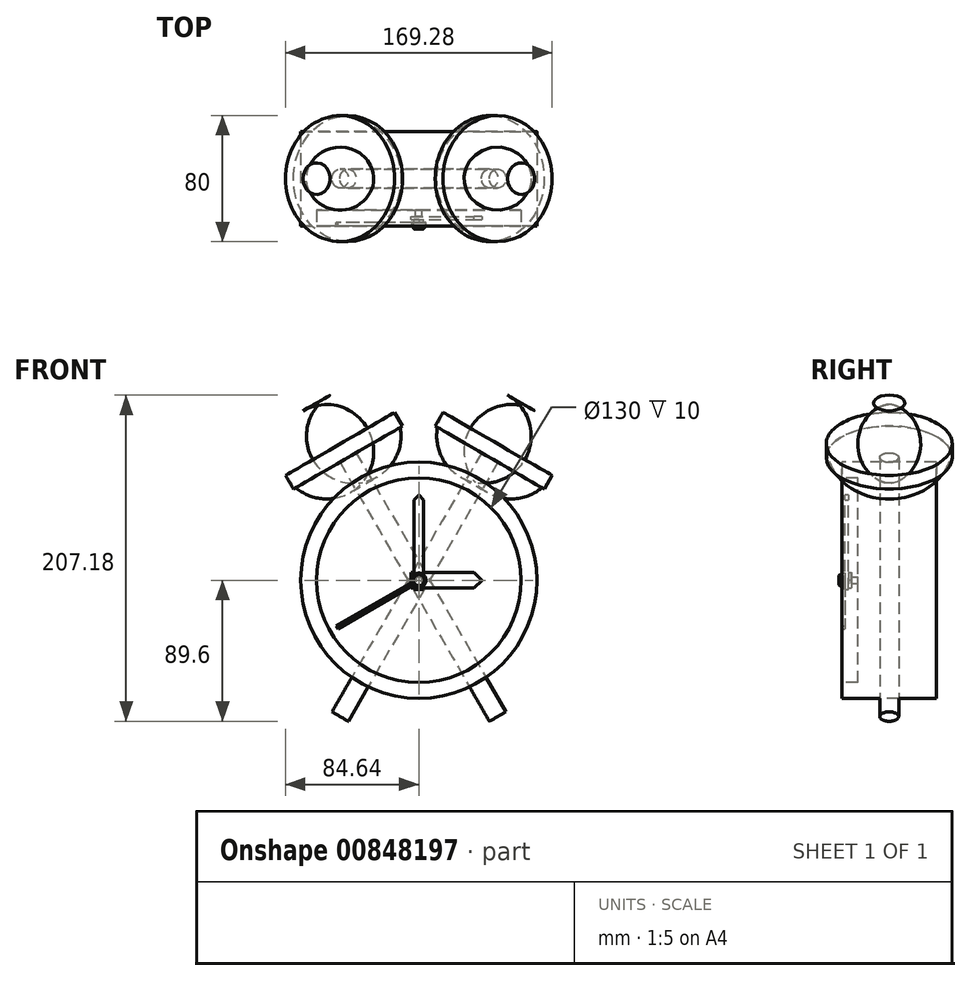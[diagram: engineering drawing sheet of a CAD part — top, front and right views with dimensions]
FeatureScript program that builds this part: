
annotation { "Feature Type Name" : "Feature", "Feature Type Description" : "" }
export const myFeature = defineFeature(function(context is Context, id is Id, definition is map)
    precondition{}
    {
        {
            var Q0;
            Q0=qCreatedBy(makeId("Front.planeOp"),FACE);
            var sketch = newSketch(context, id + "F0", { "sketchPlane" : qUnion([Q0])});
            skCircle(sketch, "E0", {"center": v(0, 0) * mm, "radius": 75 * mm});
            skSolve(sketch);
        }
        {
            var Q0;
            Q0=makeQuery(id+"F0.imprint","IMPRINT",FACE,{"disambiguationData":[TD([[makeQuery(id+"F0.imprint","IMPRINT",EDGE,{"derivedFrom":sQuery(id+"F0.wireOp",EDGE,"E0")}),1.0]])]});
            extrude(context, id + "F1", {"entities" : qUnion([Q0]), "oppositeDirection" : true, "depth" : 60 * mm, "offsetDistance" : 25 * mm});
        }
        {
            var Q0;
            Q0=makeQuery(id+"F1.opExtrude","CAP_FACE",FACE,{"disambiguationData":[OSD([sQuery(id+"F0.wireOp",EDGE,"E0")])],"isStart":true});
            var sketch = newSketch(context, id + "F2", { "sketchPlane" : qUnion([Q0])});
            skCircle(sketch, "E1", {"center": v(0, 0) * mm, "radius": 65 * mm});
            skSolve(sketch);
        }
        {
            var Q0;
            Q0=makeQuery(id+"F2.imprint","IMPRINT",FACE,{"disambiguationData":[TD([[makeQuery(id+"F2.imprint","IMPRINT",EDGE,{"derivedFrom":sQuery(id+"F2.wireOp",EDGE,"E1")}),1.0]])]});
            extrude(context, id + "F3", {"entities" : qUnion([Q0]), "operationType" : NewBodyOperationType.REMOVE, "oppositeDirection" : true, "depth" : 10 * mm, "offsetDistance" : 25 * mm});
        }
        {
            var Q0;
            Q0=makeQuery(id+"F3.boolean.opBoolean","COPY",FACE,{"derivedFrom":makeQuery(id+"F3.opExtrude","CAP_FACE",FACE,{"disambiguationData":[OSD([sQuery(id+"F2.wireOp",EDGE,"E1")])],"isStart":false})});
            var sketch = newSketch(context, id + "F4", { "sketchPlane" : qUnion([Q0])});
            skLineSegment(sketch, "E2", {"start": v(0, 0) * mm, "end": v(0, 130) * mm});
            skLineSegment(sketch, "E3", {"start": v(0, 130) * mm, "end": v(40, 130) * mm});
            skLineSegment(sketch, "E4", {"start": v(40, 130) * mm, "end": v(40, 90) * mm});
            skLineSegment(sketch, "E5", {"start": v(40, 90) * mm, "end": v(6, 90) * mm});
            skLineSegment(sketch, "E6", {"start": v(6, 90) * mm, "end": v(6, -100) * mm});
            skLineSegment(sketch, "E7", {"start": v(6, -100) * mm, "end": v(0, -100) * mm});
            skLineSegment(sketch, "E8", {"start": v(0, -100) * mm, "end": v(0, 0) * mm});
            skSolve(sketch);
        }
        {
            var Q0;
            {var subQ1=sQuery(id+"F4.wireOp",EDGE,"E3");Q0=makeQuery(id+"F4.imprint","IMPRINT",FACE,{"disambiguationData":[TD([[makeQuery(id+"F4.imprint","IMPRINT",EDGE,{"derivedFrom":subQ1}),-1.0]])]});}
            var Q1;
            {var subQ0=sQuery(id+"F4.wireOp",EDGE,"E2");var subQ6=sQuery(id+"F4.wireOp",EDGE,"E8");var subQ7=makeQuery(id+"F4.imprint","INTERSECT",VERTEX,{"derivedFrom":[subQ0,subQ6]});Q1=makeQuery(id+"F4.imprint","IMPRINT",FACE,{"disambiguationData":[TD([[makeQuery(id+"F4.imprint","IMPRINT",EDGE,{"disambiguationData":[TD([[subQ7,-1.0]])],"derivedFrom":subQ0}),-1.0]])]});}
            var Q2;
            {var subQ0=sQuery(id+"F4.wireOp",EDGE,"E7");Q2=makeQuery(id+"F4.imprint","IMPRINT",FACE,{"disambiguationData":[TD([[makeQuery(id+"F4.imprint","IMPRINT",EDGE,{"derivedFrom":subQ0}),-1.0]])]});}
            var Q3;
            Q3=sQuery(id+"F4.wireOp",EDGE,"E2");
            revolve(context, id + "F5", {"surfaceOperationType" : NewSurfaceOperationType.NEW, "entities" : qUnion([Q0, Q1, Q2]), "axis" : qUnion([Q3]), "revolveType" : RevolveType.FULL});
        }
        {
            var Q0;
            Q0=makeQuery(id+"F5.opRevolve","SWEPT_BODY",BODY,{"disambiguationData":[OSD([sQuery(id+"F4.wireOp",EDGE,"E2"),sQuery(id+"F4.wireOp",EDGE,"E3"),sQuery(id+"F4.wireOp",EDGE,"E4"),sQuery(id+"F4.wireOp",EDGE,"E5"),sQuery(id+"F4.wireOp",EDGE,"E6"),sQuery(id+"F4.wireOp",EDGE,"E7"),sQuery(id+"F4.wireOp",EDGE,"E8")])]});
            transform(context, id + "F6", {"entities" : qUnion([Q0]), "transformType" : TransformType.TRANSLATION_3D, "dx" : 0 * mm, "dy" : 20 * mm, "dz" : 0 * mm, "makeCopy" : false});
        }
        {
            var Q0;
            Q0=makeQuery(id+"F5.opRevolve","SWEPT_FACE",FACE,{"disambiguationData":[OSD([sQuery(id+"F4.wireOp",EDGE,"E3")])]});
            fillet(context, id + "F7", {"entities" : qUnion([Q0]), "radius" : 30 * mm, "allowEdgeOverflow" : false});
        }
        {
            var Q0;
            Q0=makeQuery(id+"F5.opRevolve","SWEPT_BODY",BODY,{"disambiguationData":[OSD([sQuery(id+"F4.wireOp",EDGE,"E2"),sQuery(id+"F4.wireOp",EDGE,"E3"),sQuery(id+"F4.wireOp",EDGE,"E4"),sQuery(id+"F4.wireOp",EDGE,"E5"),sQuery(id+"F4.wireOp",EDGE,"E6"),sQuery(id+"F4.wireOp",EDGE,"E7"),sQuery(id+"F4.wireOp",EDGE,"E8")])]});
            var Q1;
            Q1=makeQuery(id+"F1.opExtrude","SWEPT_FACE",FACE,{"disambiguationData":[OSD([sQuery(id+"F0.wireOp",EDGE,"E0")])]});
            transform(context, id + "F8", {"entities" : qUnion([Q0]), "transformType" : TransformType.ROTATION, "transformAxis" : qUnion([Q1]), "angle" : 30 * degree, "makeCopy" : false});
        }
        {
            var Q0;
            Q0=makeQuery(id+"F5.opRevolve","SWEPT_BODY",BODY,{"disambiguationData":[OSD([sQuery(id+"F4.wireOp",EDGE,"E2"),sQuery(id+"F4.wireOp",EDGE,"E3"),sQuery(id+"F4.wireOp",EDGE,"E4"),sQuery(id+"F4.wireOp",EDGE,"E5"),sQuery(id+"F4.wireOp",EDGE,"E6"),sQuery(id+"F4.wireOp",EDGE,"E7"),sQuery(id+"F4.wireOp",EDGE,"E8")])]});
            var Q1;
            Q1=makeQuery(id+"F1.opExtrude","CAP_EDGE",EDGE,{"disambiguationData":[OSD([sQuery(id+"F0.wireOp",EDGE,"E0")])],"isStart":true});
            transform(context, id + "F9", {"entities" : qUnion([Q0]), "transformType" : TransformType.ROTATION, "transformAxis" : qUnion([Q1]), "angle" : 300 * degree, "makeCopy" : true});
        }
        {
            var Q0;
            Q0=makeQuery(id+"F3.boolean.opBoolean","COPY",FACE,{"derivedFrom":makeQuery(id+"F3.opExtrude","CAP_FACE",FACE,{"disambiguationData":[OSD([sQuery(id+"F2.wireOp",EDGE,"E1")])],"isStart":false})});
            var sketch = newSketch(context, id + "F10", { "sketchPlane" : qUnion([Q0])});
            skCircle(sketch, "E9", {"center": v(0, 0) * mm, "radius": 2 * mm});
            skSolve(sketch);
        }
        {
            var Q0;
            Q0=makeQuery(id+"F10.imprint","IMPRINT",FACE,{"disambiguationData":[TD([[makeQuery(id+"F10.imprint","IMPRINT",EDGE,{"derivedFrom":sQuery(id+"F10.wireOp",EDGE,"E9")}),1.0]])]});
            extrude(context, id + "F11", {"entities" : qUnion([Q0]), "depth" : 4 * mm, "offsetDistance" : 25 * mm});
        }
        {
            var Q0;
            Q0=makeQuery(id+"F11.opExtrude","CAP_FACE",FACE,{"disambiguationData":[OSD([sQuery(id+"F10.wireOp",EDGE,"E9")])],"isStart":false});
            var sketch = newSketch(context, id + "F12", { "sketchPlane" : qUnion([Q0])});
            skLineSegment(sketch, "E10.bottom", {"start": v(-5, 5) * mm, "end": v(40, 5) * mm});
            skLineSegment(sketch, "E10.top", {"start": v(-5, -5) * mm, "end": v(40, -5) * mm});
            skLineSegment(sketch, "E10.left", {"start": v(-5, 5) * mm, "end": v(-5, -5) * mm});
            skLineSegment(sketch, "E10.right", {"start": v(40, 5) * mm, "end": v(40, -5) * mm});
            skSolve(sketch);
        }
        {
            var Q0;
            Q0=makeQuery(id+"F12.imprint","IMPRINT",FACE,{"disambiguationData":[TD([[makeQuery(id+"F12.imprint","IMPRINT",EDGE,{"derivedFrom":sQuery(id+"F12.wireOp",EDGE,"E10.bottom")}),-1.0]])]});
            var Q1;
            Q1=makeQuery(id+"F12.imprint","IMPRINT",FACE,{"disambiguationData":[TD([[makeQuery(id+"F12.imprint","IMPRINT",EDGE,{"derivedFrom":makeQuery(id+"F11.opExtrude","CAP_EDGE",EDGE,{"disambiguationData":[OSD([sQuery(id+"F10.wireOp",EDGE,"E9")])],"isStart":false})}),1.0]])]});
            extrude(context, id + "F13", {"entities" : qUnion([Q0, Q1]), "depth" : 2 * mm, "offsetDistance" : 25 * mm});
        }
        {
            var Q0;
            Q0=makeQuery(id+"F13.opExtrude","SWEPT_EDGE",EDGE,{"disambiguationData":[OSD([sQuery(id+"F12.wireOp",EDGE,"E10.bottom"),sQuery(id+"F12.wireOp",EDGE,"E10.right")])]});
            var Q1;
            Q1=makeQuery(id+"F13.opExtrude","SWEPT_EDGE",EDGE,{"disambiguationData":[OSD([sQuery(id+"F12.wireOp",EDGE,"E10.top"),sQuery(id+"F12.wireOp",EDGE,"E10.right")])]});
            chamfer(context, id + "F14", {"entities" : qUnion([Q0, Q1]), "width" : 5 * mm, "tangentPropagation" : true});
        }
        {
            var Q0;
            Q0=makeQuery(id+"F13.opExtrude","CAP_FACE",FACE,{"disambiguationData":[OSD([sQuery(id+"F12.wireOp",EDGE,"E10.bottom"),sQuery(id+"F12.wireOp",EDGE,"E10.top"),sQuery(id+"F12.wireOp",EDGE,"E10.left"),sQuery(id+"F12.wireOp",EDGE,"E10.right")])],"isStart":false});
            var sketch = newSketch(context, id + "F15", { "sketchPlane" : qUnion([Q0])});
            skLineSegment(sketch, "E11.bottom", {"start": v(-3, -6) * mm, "end": v(3, -6) * mm});
            skLineSegment(sketch, "E11.top", {"start": v(-3, 54) * mm, "end": v(3, 54) * mm});
            skLineSegment(sketch, "E11.left", {"start": v(-3, -6) * mm, "end": v(-3, 54) * mm});
            skLineSegment(sketch, "E11.right", {"start": v(3, -6) * mm, "end": v(3, 54) * mm});
            skSolve(sketch);
        }
        {
            var Q0;
            {var subQ0=sQuery(id+"F15.wireOp",EDGE,"E11.top");Q0=makeQuery(id+"F15.imprint","IMPRINT",FACE,{"disambiguationData":[TD([[makeQuery(id+"F15.imprint","IMPRINT",EDGE,{"derivedFrom":subQ0}),-1.0]])]});}
            var Q1;
            {var subQ0=sQuery(id+"F15.wireOp",EDGE,"E11.left");var subQ1=makeQuery(id+"F13.opExtrude","CAP_EDGE",EDGE,{"disambiguationData":[OSD([sQuery(id+"F12.wireOp",EDGE,"E10.top")])],"isStart":false});var subQ2=makeQuery(id+"F15.imprint","INTERSECT",VERTEX,{"derivedFrom":[subQ1,subQ0]});Q1=makeQuery(id+"F15.imprint","IMPRINT",FACE,{"disambiguationData":[TD([[makeQuery(id+"F15.imprint","IMPRINT",EDGE,{"disambiguationData":[TD([[subQ2,-1.0]])],"derivedFrom":subQ0}),-1.0]])]});}
            var Q2;
            {var subQ0=sQuery(id+"F15.wireOp",EDGE,"E11.bottom");Q2=makeQuery(id+"F15.imprint","IMPRINT",FACE,{"disambiguationData":[TD([[makeQuery(id+"F15.imprint","IMPRINT",EDGE,{"derivedFrom":subQ0}),1.0]])]});}
            extrude(context, id + "F16", {"entities" : qUnion([Q0, Q1, Q2]), "depth" : 2 * mm, "offsetDistance" : 25 * mm});
        }
        {
            var Q0;
            Q0=makeQuery(id+"F16.opExtrude","SWEPT_EDGE",EDGE,{"disambiguationData":[OSD([sQuery(id+"F15.wireOp",EDGE,"E11.top"),sQuery(id+"F15.wireOp",EDGE,"E11.right")])]});
            var Q1;
            Q1=makeQuery(id+"F16.opExtrude","SWEPT_EDGE",EDGE,{"disambiguationData":[OSD([sQuery(id+"F15.wireOp",EDGE,"E11.top"),sQuery(id+"F15.wireOp",EDGE,"E11.left")])]});
            chamfer(context, id + "F17", {"entities" : qUnion([Q0, Q1]), "width" : 3 * mm, "tangentPropagation" : true});
        }
        {
            var Q0;
            Q0=makeQuery(id+"F16.opExtrude","CAP_FACE",FACE,{"disambiguationData":[OSD([sQuery(id+"F15.wireOp",EDGE,"E11.bottom"),sQuery(id+"F15.wireOp",EDGE,"E11.top"),sQuery(id+"F15.wireOp",EDGE,"E11.left"),sQuery(id+"F15.wireOp",EDGE,"E11.right")])],"isStart":false});
            var sketch = newSketch(context, id + "F18", { "sketchPlane" : qUnion([Q0])});
            skArc(sketch, "E12", {"start": v(1, -4.39) * mm, "mid": v(0, 4.5) * mm, "end": v(-1, -4.39) * mm});
            skLineSegment(sketch, "E13.top", {"start": v(-1, -60) * mm, "end": v(1, -60) * mm});
            skLineSegment(sketch, "E13.left", {"start": v(-1, -4.39) * mm, "end": v(-1, -60) * mm});
            skLineSegment(sketch, "E13.right", {"start": v(1, -4.39) * mm, "end": v(1, -60) * mm});
            skSolve(sketch);
        }
        {
            var Q0;
            {var subQ1=sQuery(id+"F18.wireOp",EDGE,"E12");var subQ10=sQuery(id+"F18.wireOp",EDGE,"E13.right");var subQ11=makeQuery(id+"F18.imprint","INTERSECT",VERTEX,{"derivedFrom":[subQ1,subQ10]});Q0=makeQuery(id+"F18.imprint","IMPRINT",FACE,{"disambiguationData":[TD([[makeQuery(id+"F18.imprint","IMPRINT",EDGE,{"disambiguationData":[TD([[subQ11,-1.0]])],"derivedFrom":subQ1}),1.0]])]});}
            var Q1;
            {var subQ0=sQuery(id+"F18.wireOp",EDGE,"E12");var subQ1=makeQuery(id+"F16.opExtrude","CAP_EDGE",EDGE,{"disambiguationData":[OSD([sQuery(id+"F15.wireOp",EDGE,"E11.left")])],"isStart":false});var subQ2=makeQuery(id+"F18.imprint","INTERSECT",VERTEX,{"disambiguationData":[OD(0.0)],"derivedFrom":[subQ1,subQ0]});Q1=makeQuery(id+"F18.imprint","IMPRINT",FACE,{"disambiguationData":[TD([[makeQuery(id+"F18.imprint","IMPRINT",EDGE,{"disambiguationData":[TD([[subQ2,-1.0]])],"derivedFrom":subQ0}),1.0]])]});}
            var Q2;
            {var subQ0=sQuery(id+"F18.wireOp",EDGE,"E12");var subQ1=makeQuery(id+"F16.opExtrude","CAP_EDGE",EDGE,{"disambiguationData":[OSD([sQuery(id+"F15.wireOp",EDGE,"E11.right")])],"isStart":false});var subQ2=makeQuery(id+"F18.imprint","INTERSECT",VERTEX,{"disambiguationData":[OD(0.0)],"derivedFrom":[subQ1,subQ0]});Q2=makeQuery(id+"F18.imprint","IMPRINT",FACE,{"disambiguationData":[TD([[makeQuery(id+"F18.imprint","IMPRINT",EDGE,{"disambiguationData":[TD([[subQ2,-1.0]])],"derivedFrom":subQ0}),1.0]])]});}
            var Q3;
            {var subQ0=sQuery(id+"F18.wireOp",EDGE,"E13.top");Q3=makeQuery(id+"F18.imprint","IMPRINT",FACE,{"disambiguationData":[TD([[makeQuery(id+"F18.imprint","IMPRINT",EDGE,{"derivedFrom":subQ0}),1.0]])]});}
            extrude(context, id + "F19", {"entities" : qUnion([Q0, Q1, Q2, Q3]), "depth" : 2 * mm, "offsetDistance" : 25 * mm});
        }
        {
            var Q0;
            Q0=makeQuery(id+"F19.opExtrude","SWEPT_BODY",BODY,{"disambiguationData":[OSD([sQuery(id+"F18.wireOp",EDGE,"E12"),sQuery(id+"F18.wireOp",EDGE,"E13.top"),sQuery(id+"F18.wireOp",EDGE,"E13.left"),sQuery(id+"F18.wireOp",EDGE,"E13.right")])]});
            var Q1;
            Q1=makeQuery(id+"F1.opExtrude","SWEPT_FACE",FACE,{"disambiguationData":[OSD([sQuery(id+"F0.wireOp",EDGE,"E0")])]});
            transform(context, id + "F20", {"entities" : qUnion([Q0]), "transformType" : TransformType.ROTATION, "transformAxis" : qUnion([Q1]), "angle" : 300 * degree, "makeCopy" : false});
        }
        {
            var Q0;
            Q0=makeQuery(id+"F19.opExtrude","CAP_FACE",FACE,{"disambiguationData":[OSD([sQuery(id+"F18.wireOp",EDGE,"E12"),sQuery(id+"F18.wireOp",EDGE,"E13.top"),sQuery(id+"F18.wireOp",EDGE,"E13.left"),sQuery(id+"F18.wireOp",EDGE,"E13.right")])],"isStart":false});
            var sketch = newSketch(context, id + "F21", { "sketchPlane" : qUnion([Q0])});
            skCircle(sketch, "E14", {"center": v(0, 0) * mm, "radius": 3.5 * mm});
            skSolve(sketch);
        }
        {
            var Q0;
            Q0=makeQuery(id+"F21.imprint","IMPRINT",FACE,{"disambiguationData":[TD([[makeQuery(id+"F21.imprint","IMPRINT",EDGE,{"derivedFrom":sQuery(id+"F21.wireOp",EDGE,"E14")}),1.0]])]});
            extrude(context, id + "F22", {"entities" : qUnion([Q0]), "depth" : 2 * mm, "offsetDistance" : 25 * mm});
        }
        {
            var Q0;
            Q0=makeQuery(id+"F22.opExtrude","CAP_EDGE",EDGE,{"disambiguationData":[OSD([sQuery(id+"F21.wireOp",EDGE,"E14")])],"isStart":false});
            fillet(context, id + "F23", {"entities" : qUnion([Q0]), "radius" : 1 * mm, "tangentPropagation" : true, "allowEdgeOverflow" : false});
        }
    });
